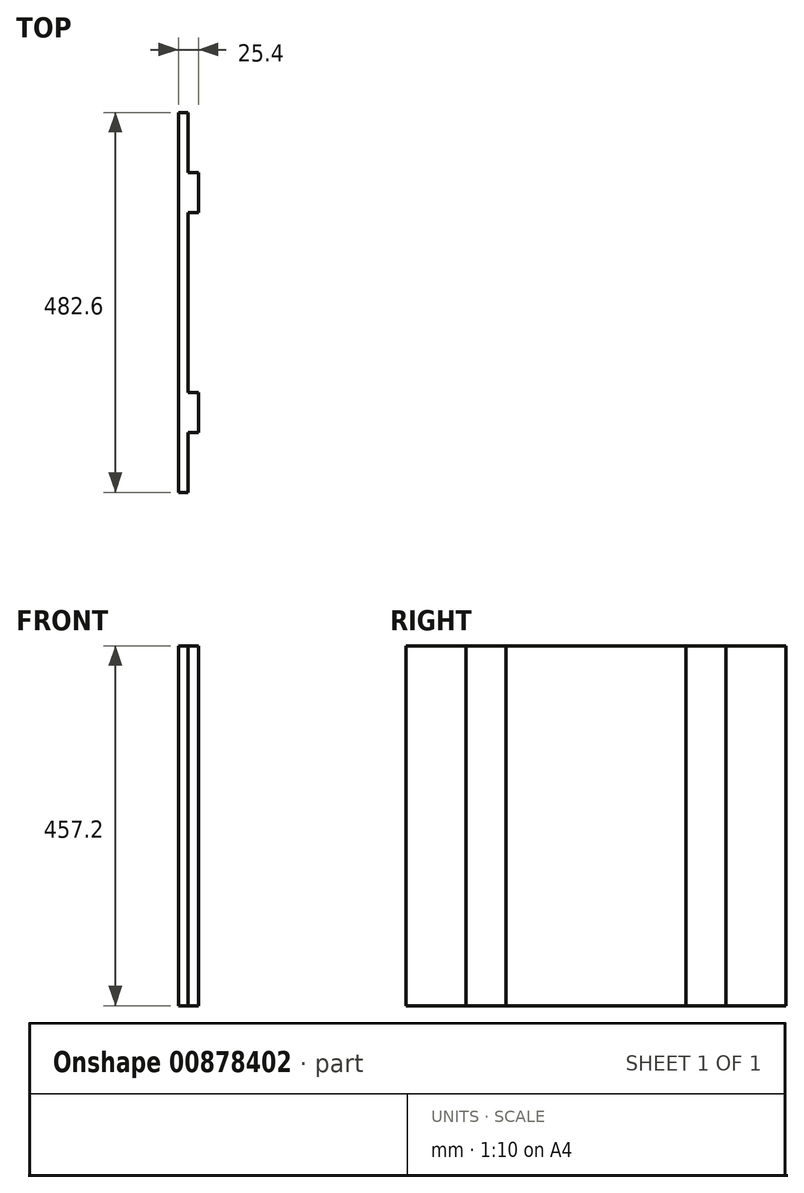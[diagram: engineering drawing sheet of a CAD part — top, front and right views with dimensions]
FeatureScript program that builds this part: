
annotation { "Feature Type Name" : "Feature", "Feature Type Description" : "" }
export const myFeature = defineFeature(function(context is Context, id is Id, definition is map)
    precondition{}
    {
        {
            var Q0;
            Q0=qCreatedBy(makeId("Right.planeOp"),FACE);
            var sketch = newSketch(context, id + "F0", { "sketchPlane" : qUnion([Q0])});
            skLineSegment(sketch, "E0.bottom", {"start": v(0, 0) * mm, "end": v(482.6, 0) * mm});
            skLineSegment(sketch, "E0.top", {"start": v(0, 457.2) * mm, "end": v(482.6, 457.2) * mm});
            skLineSegment(sketch, "E0.left", {"start": v(0, 0) * mm, "end": v(0, 457.2) * mm});
            skLineSegment(sketch, "E0.right", {"start": v(482.6, 0) * mm, "end": v(482.6, 457.2) * mm});
            skSolve(sketch);
        }
        {
            var Q0;
            Q0=makeQuery(id+"F0.imprint","IMPRINT",FACE,{"disambiguationData":[TD([[makeQuery(id+"F0.imprint","IMPRINT",EDGE,{"derivedFrom":sQuery(id+"F0.wireOp",EDGE,"E0.bottom")}),1.0]])]});
            extrude(context, id + "F1", {"entities" : qUnion([Q0]), "depth" : 12.7 * mm, "offsetDistance" : 25.4 * mm});
        }
        {
            var Q0;
            Q0=makeQuery(id+"F1.opExtrude","CAP_FACE",FACE,{"disambiguationData":[OSD([sQuery(id+"F0.wireOp",EDGE,"E0.bottom"),sQuery(id+"F0.wireOp",EDGE,"E0.top"),sQuery(id+"F0.wireOp",EDGE,"E0.left"),sQuery(id+"F0.wireOp",EDGE,"E0.right")])],"isStart":false});
            var sketch = newSketch(context, id + "F2", { "sketchPlane" : qUnion([Q0])});
            skLineSegment(sketch, "E1.bottom", {"start": v(76.2, 457.2) * mm, "end": v(127, 457.2) * mm});
            skLineSegment(sketch, "E1.top", {"start": v(76.2, 0) * mm, "end": v(127, 0) * mm});
            skLineSegment(sketch, "E1.left", {"start": v(76.2, 457.2) * mm, "end": v(76.2, 0) * mm});
            skLineSegment(sketch, "E1.right", {"start": v(127, 457.2) * mm, "end": v(127, 0) * mm});
            skLineSegment(sketch, "E2.bottom", {"start": v(406.4, 457.2) * mm, "end": v(355.6, 457.2) * mm});
            skLineSegment(sketch, "E2.top", {"start": v(406.4, 0) * mm, "end": v(355.6, 0) * mm});
            skLineSegment(sketch, "E2.left", {"start": v(406.4, 457.2) * mm, "end": v(406.4, 0) * mm});
            skLineSegment(sketch, "E2.right", {"start": v(355.6, 457.2) * mm, "end": v(355.6, 0) * mm});
            skSolve(sketch);
        }
        {
            var Q0;
            Q0 = qSketchRegion(id + "F2", true);
            extrude(context, id + "F3", {"entities" : qUnion([Q0]), "operationType" : NewBodyOperationType.ADD, "depth" : 12.7 * mm, "offsetDistance" : 25.4 * mm});
        }
    });
